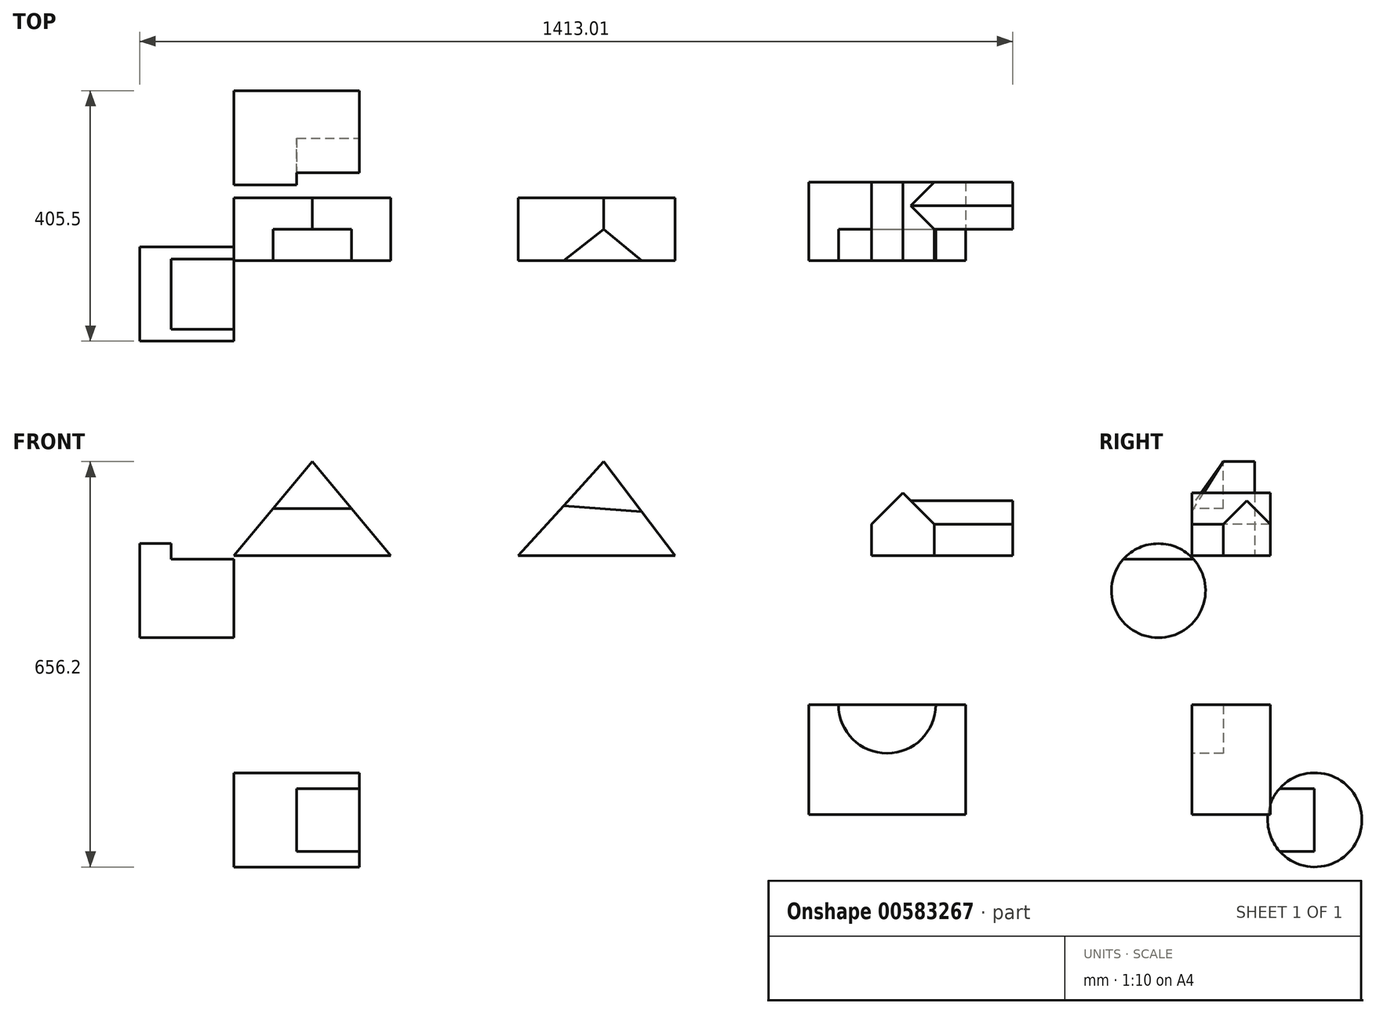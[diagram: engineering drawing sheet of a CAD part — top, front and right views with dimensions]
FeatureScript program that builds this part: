
annotation { "Feature Type Name" : "Feature", "Feature Type Description" : "" }
export const myFeature = defineFeature(function(context is Context, id is Id, definition is map)
    precondition{}
    {
        {
            var Q0;
            Q0=qCreatedBy(makeId("Front.planeOp"),FACE);
            var sketch = newSketch(context, id + "F0", { "sketchPlane" : qUnion([Q0])});
            skLineSegment(sketch, "E0", {"start": v(0, 0) * mm, "end": v(127, 152.4) * mm});
            skLineSegment(sketch, "E1", {"start": v(127, 152.4) * mm, "end": v(254, 0) * mm});
            skLineSegment(sketch, "E2", {"start": v(254, 0) * mm, "end": v(0, 0) * mm});
            skSolve(sketch);
        }
        {
            var Q0;
            Q0=makeQuery(id+"F0.imprint","IMPRINT",FACE,{"disambiguationData":[TD([[makeQuery(id+"F0.imprint","IMPRINT",EDGE,{"derivedFrom":sQuery(id+"F0.wireOp",EDGE,"E0")}),-1.0]])]});
            extrude(context, id + "F1", {"entities" : qUnion([Q0]), "oppositeDirection" : true, "depth" : 101.6 * mm, "offsetDistance" : 25.4 * mm});
        }
        {
            var Q0;
            Q0=makeQuery(id+"F1.opExtrude","CAP_FACE",FACE,{"disambiguationData":[OSD([sQuery(id+"F0.wireOp",EDGE,"E0"),sQuery(id+"F0.wireOp",EDGE,"E1"),sQuery(id+"F0.wireOp",EDGE,"E2")])],"isStart":true});
            var sketch = newSketch(context, id + "F2", { "sketchPlane" : qUnion([Q0])});
            skLineSegment(sketch, "E3", {"start": v(63.5, 76.2) * mm, "end": v(190.5, 76.2) * mm});
            skLineSegment(sketch, "E4", {"start": v(190.5, 76.2) * mm, "end": v(127, 152.4) * mm});
            skLineSegment(sketch, "E5", {"start": v(127, 152.4) * mm, "end": v(63.5, 76.2) * mm});
            skSolve(sketch);
        }
        {
            var Q0;
            Q0=makeQuery(id+"F2.imprint","IMPRINT",FACE,{"disambiguationData":[TD([[makeQuery(id+"F2.imprint","IMPRINT",EDGE,{"derivedFrom":sQuery(id+"F2.wireOp",EDGE,"E3")}),1.0]])]});
            extrude(context, id + "F3", {"entities" : qUnion([Q0]), "operationType" : NewBodyOperationType.REMOVE, "oppositeDirection" : true, "depth" : 50.8 * mm, "offsetDistance" : 25.4 * mm});
        }
        {
            var Q0;
            Q0=qCreatedBy(makeId("Front.planeOp"),FACE);
            var sketch = newSketch(context, id + "F4", { "sketchPlane" : qUnion([Q0])});
            skLineSegment(sketch, "E6", {"start": v(459.92, 0) * mm, "end": v(598.7, 152.4) * mm});
            skLineSegment(sketch, "E7", {"start": v(598.7, 152.4) * mm, "end": v(713.92, 0) * mm});
            skLineSegment(sketch, "E8", {"start": v(713.92, 0) * mm, "end": v(459.92, 0) * mm});
            skSolve(sketch);
        }
        {
            var Q0;
            Q0=makeQuery(id+"F4.imprint","IMPRINT",FACE,{"disambiguationData":[TD([[makeQuery(id+"F4.imprint","IMPRINT",EDGE,{"derivedFrom":sQuery(id+"F4.wireOp",EDGE,"E6")}),-1.0]])]});
            extrude(context, id + "F5", {"entities" : qUnion([Q0]), "oppositeDirection" : true, "depth" : 101.6 * mm, "offsetDistance" : 25.4 * mm});
        }
        {
            var Q0;
            Q0=makeQuery(id+"F5.opExtrude","CAP_EDGE",EDGE,{"disambiguationData":[OSD([sQuery(id+"F4.wireOp",EDGE,"E8")])],"isStart":true});
            cPoint(context, id + "F6", {"entities" : qUnion([Q0]), "parameter" : 0.5});
        }
        {
            var Q0;
            Q0=makeQuery(id+"F5.opExtrude","CAP_VERTEX",VERTEX,{"disambiguationData":[OSD([sQuery(id+"F4.wireOp",EDGE,"E6"),sQuery(id+"F4.wireOp",EDGE,"E7")])],"isStart":true});
            var Q1;
            Q1=makeQuery(id+"F5.opExtrude","CAP_VERTEX",VERTEX,{"disambiguationData":[OSD([sQuery(id+"F4.wireOp",EDGE,"E6"),sQuery(id+"F4.wireOp",EDGE,"E7")])],"isStart":false});
            var Q2;
            Q2 = qCreatedBy(id + "F6" ,VERTEX);
            cPlane(context, id + "F7", {"entities" : qUnion([Q0, Q1, Q2]), "cplaneType" : CPlaneType.THREE_POINT, "offset" : 25.4 * mm, "width" : 152.4 * mm, "height" : 152.4 * mm});
        }
        {
            var Q0;
            Q0=qCreatedBy(id+"F7.planeOp",FACE);
            var sketch = newSketch(context, id + "F8", { "sketchPlane" : qUnion([Q0])});
            skLineSegment(sketch, "E9.0.0", {"start": v(0, 198.1) * mm, "end": v(0, 121.9) * mm});
            skLineSegment(sketch, "E9.0.3", {"start": v(50.8, 198.1) * mm, "end": v(0, 198.1) * mm});
            skLineSegment(sketch, "E10", {"start": v(0, 121.9) * mm, "end": v(50.8, 198.1) * mm});
            skPoint(sketch, "E11.orphan", {"position": v(0, 55.04) * mm});
            skPoint(sketch, "E12.orphan", {"position": v(101.6, 198.1) * mm});
            skSolve(sketch);
        }
        {
            var Q0;
            Q0 = qSketchRegion(id + "F8", true);
            extrude(context, id + "F9", {"entities" : qUnion([Q0]), "operationType" : NewBodyOperationType.REMOVE, "endBound" : BoundingType.SYMMETRIC, "depth" : 152.4 * mm, "offsetDistance" : 25.4 * mm});
        }
        {
            var Q0;
            Q0=qCreatedBy(makeId("Front.planeOp"),FACE);
            var sketch = newSketch(context, id + "F10", { "sketchPlane" : qUnion([Q0])});
            skLineSegment(sketch, "E13", {"start": v(1032, 0) * mm, "end": v(1032, 50.8) * mm});
            skLineSegment(sketch, "E14", {"start": v(1032, 50.8) * mm, "end": v(1082.8, 101.6) * mm});
            skLineSegment(sketch, "E15", {"start": v(1082.8, 101.6) * mm, "end": v(1133.6, 50.8) * mm});
            skLineSegment(sketch, "E16", {"start": v(1133.6, 50.8) * mm, "end": v(1133.6, 0) * mm});
            skLineSegment(sketch, "E17", {"start": v(1133.6, 0) * mm, "end": v(1032, 0) * mm});
            skSolve(sketch);
        }
        {
            var Q0;
            Q0=makeQuery(id+"F10.imprint","IMPRINT",FACE,{"disambiguationData":[TD([[makeQuery(id+"F10.imprint","IMPRINT",EDGE,{"derivedFrom":sQuery(id+"F10.wireOp",EDGE,"E13")}),-1.0]])]});
            extrude(context, id + "F11", {"entities" : qUnion([Q0]), "oppositeDirection" : true, "depth" : 127 * mm, "offsetDistance" : 25.4 * mm});
        }
        {
            var Q0;
            Q0=makeQuery(id+"F11.opExtrude","SWEPT_FACE",FACE,{"disambiguationData":[OSD([sQuery(id+"F10.wireOp",EDGE,"E16")])]});
            cPlane(context, id + "F12", {"entities" : qUnion([Q0]), "cplaneType" : CPlaneType.OFFSET, "offset" : 127 * mm, "width" : 152.4 * mm, "height" : 152.4 * mm});
        }
        {
            var Q0;
            Q0=qCreatedBy(id+"F12.planeOp",FACE);
            var sketch = newSketch(context, id + "F13", { "sketchPlane" : qUnion([Q0])});
            skLineSegment(sketch, "E18", {"start": v(127, 0) * mm, "end": v(127, 50.8) * mm});
            skLineSegment(sketch, "E19", {"start": v(127, 50.8) * mm, "end": v(88.9, 88.9) * mm});
            skLineSegment(sketch, "E20", {"start": v(88.9, 88.9) * mm, "end": v(50.8, 50.8) * mm});
            skLineSegment(sketch, "E21", {"start": v(50.8, 50.8) * mm, "end": v(50.8, 0) * mm});
            skLineSegment(sketch, "E22", {"start": v(50.8, 0) * mm, "end": v(127, 0) * mm});
            skSolve(sketch);
        }
        {
            var Q0;
            Q0=makeQuery(id+"F13.imprint","IMPRINT",FACE,{"disambiguationData":[TD([[makeQuery(id+"F13.imprint","IMPRINT",EDGE,{"derivedFrom":sQuery(id+"F13.wireOp",EDGE,"E18")}),1.0]])]});
            extrude(context, id + "F14", {"entities" : qUnion([Q0]), "operationType" : NewBodyOperationType.ADD, "endBound" : BoundingType.UP_TO_NEXT, "oppositeDirection" : true, "depth" : 127 * mm, "offsetDistance" : 25.4 * mm});
        }
        {
            var Q0;
            Q0=qCreatedBy(makeId("Right.planeOp"),FACE);
            var sketch = newSketch(context, id + "F15", { "sketchPlane" : qUnion([Q0])});
            skCircle(sketch, "E23", {"center": v(-54.23, -56.6) * mm, "radius": 76.2 * mm});
            skSolve(sketch);
        }
        {
            var Q0;
            Q0=makeQuery(id+"F15.imprint","IMPRINT",FACE,{"disambiguationData":[TD([[makeQuery(id+"F15.imprint","IMPRINT",EDGE,{"derivedFrom":sQuery(id+"F15.wireOp",EDGE,"E23")}),1.0]])]});
            extrude(context, id + "F16", {"entities" : qUnion([Q0]), "oppositeDirection" : true, "depth" : 152.4 * mm, "offsetDistance" : 25.4 * mm});
        }
        {
            var Q0;
            Q0=makeQuery(id+"F16.opExtrude","CAP_FACE",FACE,{"disambiguationData":[OSD([sQuery(id+"F15.wireOp",EDGE,"E23")])],"isStart":true});
            var sketch = newSketch(context, id + "F17", { "sketchPlane" : qUnion([Q0])});
            skLineSegment(sketch, "E24", {"start": v(-111.02, -5.8) * mm, "end": v(2.57, -5.8) * mm});
            skSolve(sketch);
        }
        {
            var Q0;
            Q0 = qSketchRegion(id + "F17", true);
            var Q1;
            {var subQ0=sQuery(id+"F17.wireOp",EDGE,"E24");Q1=makeQuery(id+"F17.imprint","IMPRINT",FACE,{"disambiguationData":[TD([[makeQuery(id+"F17.imprint","IMPRINT",EDGE,{"derivedFrom":subQ0}),1.0]])]});}
            extrude(context, id + "F18", {"entities" : qUnion([Q0, Q1]), "operationType" : NewBodyOperationType.REMOVE, "oppositeDirection" : true, "depth" : 101.6 * mm, "offsetDistance" : 25.4 * mm});
        }
        {
            var Q0;
            Q0=qCreatedBy(makeId("Right.planeOp"),FACE);
            var sketch = newSketch(context, id + "F19", { "sketchPlane" : qUnion([Q0])});
            skCircle(sketch, "E25", {"center": v(198.85, -427.58) * mm, "radius": 76.22 * mm});
            skSolve(sketch);
        }
        {
            var Q0;
            Q0=makeQuery(id+"F19.imprint","IMPRINT",FACE,{"disambiguationData":[TD([[makeQuery(id+"F19.imprint","IMPRINT",EDGE,{"derivedFrom":sQuery(id+"F19.wireOp",EDGE,"E25")}),1.0]])]});
            extrude(context, id + "F20", {"entities" : qUnion([Q0]), "depth" : 203.2 * mm, "offsetDistance" : 25.4 * mm});
        }
        {
            var Q0;
            Q0=makeQuery(id+"F20.opExtrude","CAP_FACE",FACE,{"disambiguationData":[OSD([sQuery(id+"F19.wireOp",EDGE,"E25")])],"isStart":false});
            var sketch = newSketch(context, id + "F21", { "sketchPlane" : qUnion([Q0])});
            skLineSegment(sketch, "E26", {"start": v(142, -376.8) * mm, "end": v(197.88, -376.8) * mm});
            skLineSegment(sketch, "E27", {"start": v(197.88, -376.8) * mm, "end": v(197.88, -478.4) * mm});
            skLineSegment(sketch, "E28", {"start": v(197.88, -478.4) * mm, "end": v(142.04, -478.4) * mm});
            skSolve(sketch);
        }
        {
            var Q0;
            {var subQ0=sQuery(id+"F21.wireOp",EDGE,"E26");Q0=makeQuery(id+"F21.imprint","IMPRINT",FACE,{"disambiguationData":[TD([[makeQuery(id+"F21.imprint","IMPRINT",EDGE,{"derivedFrom":subQ0}),-1.0]])]});}
            extrude(context, id + "F22", {"entities" : qUnion([Q0]), "operationType" : NewBodyOperationType.REMOVE, "oppositeDirection" : true, "depth" : 101.6 * mm, "offsetDistance" : 25.4 * mm});
        }
        {
            var Q0;
            Q0=qCreatedBy(makeId("Front.planeOp"),FACE);
            var sketch = newSketch(context, id + "F23", { "sketchPlane" : qUnion([Q0])});
            skLineSegment(sketch, "E29.bottom", {"start": v(930.46, -241.09) * mm, "end": v(1184.46, -241.09) * mm});
            skLineSegment(sketch, "E29.top", {"start": v(930.46, -418.89) * mm, "end": v(1184.46, -418.89) * mm});
            skLineSegment(sketch, "E29.left", {"start": v(930.46, -241.09) * mm, "end": v(930.46, -418.89) * mm});
            skLineSegment(sketch, "E29.right", {"start": v(1184.46, -241.09) * mm, "end": v(1184.46, -418.89) * mm});
            skSolve(sketch);
        }
        {
            var Q0;
            Q0=makeQuery(id+"F23.imprint","IMPRINT",FACE,{"disambiguationData":[TD([[makeQuery(id+"F23.imprint","IMPRINT",EDGE,{"derivedFrom":sQuery(id+"F23.wireOp",EDGE,"E29.bottom")}),-1.0]])]});
            extrude(context, id + "F24", {"entities" : qUnion([Q0]), "oppositeDirection" : true, "depth" : 127 * mm, "offsetDistance" : 25.4 * mm});
        }
        {
            var Q0;
            Q0=makeQuery(id+"F24.opExtrude","CAP_FACE",FACE,{"disambiguationData":[OSD([sQuery(id+"F23.wireOp",EDGE,"E29.bottom"),sQuery(id+"F23.wireOp",EDGE,"E29.top"),sQuery(id+"F23.wireOp",EDGE,"E29.left"),sQuery(id+"F23.wireOp",EDGE,"E29.right")])],"isStart":true});
            var sketch = newSketch(context, id + "F25", { "sketchPlane" : qUnion([Q0])});
            skCircle(sketch, "E30", {"center": v(1057.46, -241.09) * mm, "radius": 78.76 * mm});
            skSolve(sketch);
        }
        {
            var Q0;
            {var subQ0=sQuery(id+"F25.wireOp",EDGE,"E30");var subQ1=makeQuery(id+"F24.opExtrude","CAP_EDGE",EDGE,{"disambiguationData":[OSD([sQuery(id+"F23.wireOp",EDGE,"E29.bottom")])],"isStart":true});var subQ2=makeQuery(id+"F25.imprint","INTERSECT",VERTEX,{"disambiguationData":[OD(0.0)],"derivedFrom":[subQ1,subQ0]});Q0=makeQuery(id+"F25.imprint","IMPRINT",FACE,{"disambiguationData":[TD([[makeQuery(id+"F25.imprint","IMPRINT",EDGE,{"disambiguationData":[TD([[subQ2,-1.0]])],"derivedFrom":subQ0}),1.0]])]});}
            extrude(context, id + "F26", {"entities" : qUnion([Q0]), "operationType" : NewBodyOperationType.REMOVE, "oppositeDirection" : true, "depth" : 50.8 * mm, "offsetDistance" : 25.4 * mm});
        }
    });
